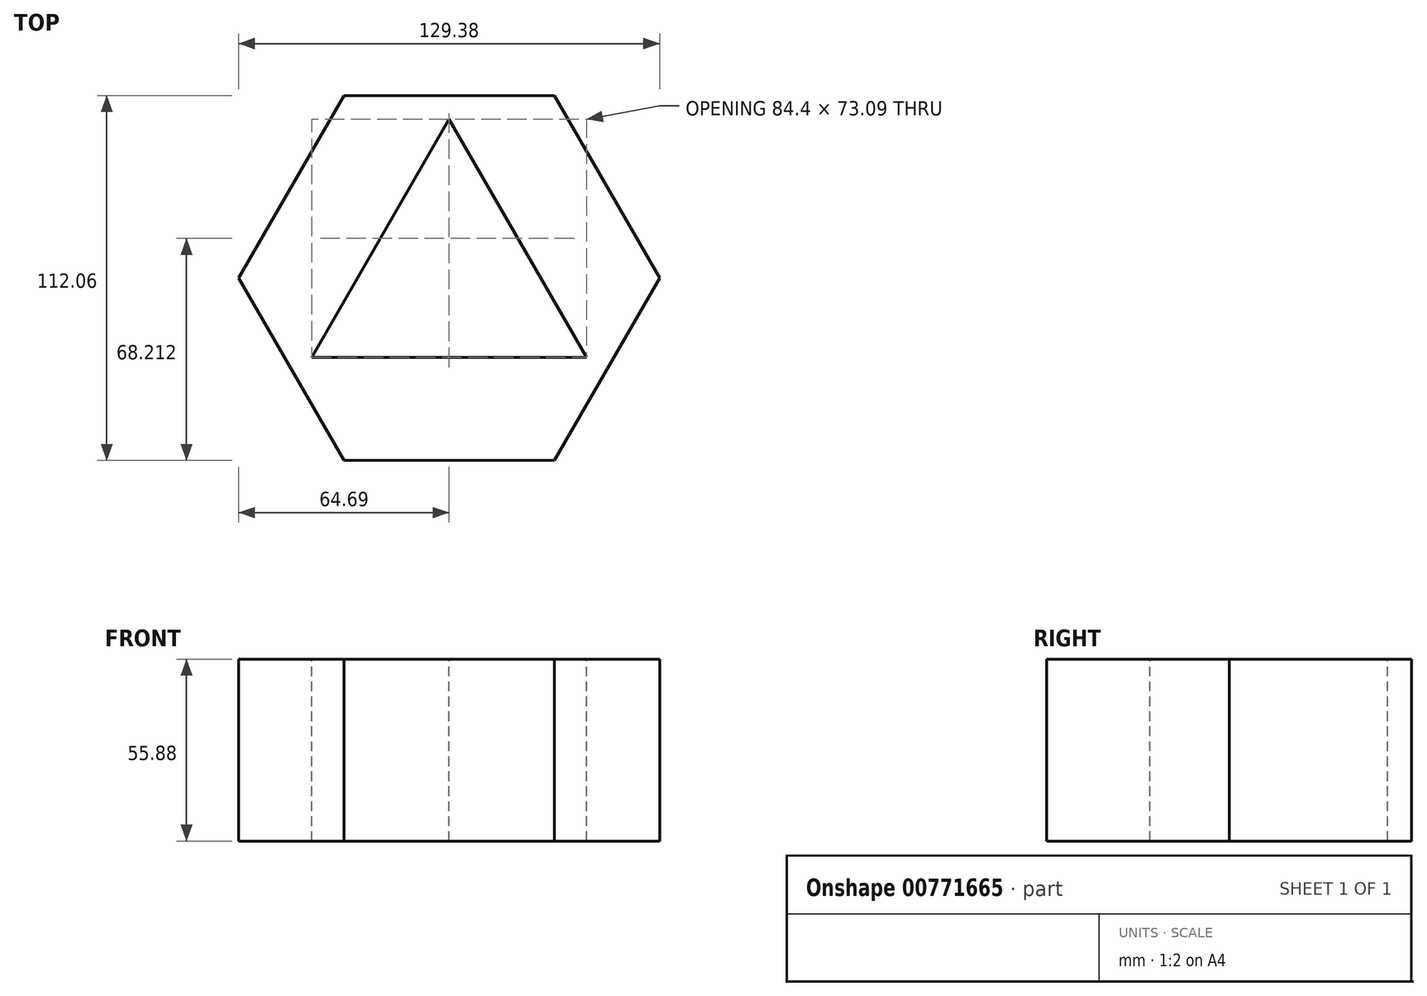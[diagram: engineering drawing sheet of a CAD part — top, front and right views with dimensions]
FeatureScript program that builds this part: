
annotation { "Feature Type Name" : "Feature", "Feature Type Description" : "" }
export const myFeature = defineFeature(function(context is Context, id is Id, definition is map)
    precondition{}
    {
        {
            var Q0;
            Q0=qCreatedBy(makeId("Top.planeOp"),FACE);
            var sketch = newSketch(context, id + "F0", { "sketchPlane" : qUnion([Q0])});
            skCircle(sketch, "E0.cCircle", {"center": v(0, 0) * mm, "radius": 56.03 * mm, "construction": true});
            skLineSegment(sketch, "E0.0", {"start": v(32.35, -56.03) * mm, "end": v(-32.35, -56.03) * mm});
            skLineSegment(sketch, "E0.1", {"start": v(-32.35, -56.03) * mm, "end": v(-64.7, 0) * mm});
            skLineSegment(sketch, "E0.2", {"start": v(-64.7, 0) * mm, "end": v(-32.35, 56.03) * mm});
            skLineSegment(sketch, "E0.3", {"start": v(-32.35, 56.03) * mm, "end": v(32.35, 56.03) * mm});
            skLineSegment(sketch, "E0.4", {"start": v(32.35, 56.03) * mm, "end": v(64.7, 0) * mm});
            skLineSegment(sketch, "E0.5", {"start": v(64.7, 0) * mm, "end": v(32.35, -56.03) * mm});
            skPoint(sketch, "E0.0.midPoint", {"position": v(0, -56.03) * mm});
            skSolve(sketch);
        }
        {
            var Q0;
            Q0 = qSketchRegion(id + "F0", true);
            extrude(context, id + "F1", {"entities" : qUnion([Q0]), "depth" : 55.88 * mm, "offsetDistance" : 25.4 * mm});
        }
        {
            var Q0;
            Q0=makeQuery(id+"F1.opExtrude","CAP_FACE",FACE,{"disambiguationData":[OSD([sQuery(id+"F0.wireOp",EDGE,"E0.0"),sQuery(id+"F0.wireOp",EDGE,"E0.1"),sQuery(id+"F0.wireOp",EDGE,"E0.2"),sQuery(id+"F0.wireOp",EDGE,"E0.3"),sQuery(id+"F0.wireOp",EDGE,"E0.4"),sQuery(id+"F0.wireOp",EDGE,"E0.5")])],"isStart":false});
            var sketch = newSketch(context, id + "F2", { "sketchPlane" : qUnion([Q0])});
            skCircle(sketch, "E1.cCircle", {"center": v(0, 0) * mm, "radius": 24.36 * mm, "construction": true});
            skLineSegment(sketch, "E1.0", {"start": v(42.2, -24.36) * mm, "end": v(-42.2, -24.36) * mm});
            skLineSegment(sketch, "E1.1", {"start": v(-42.2, -24.36) * mm, "end": v(0, 48.73) * mm});
            skLineSegment(sketch, "E1.2", {"start": v(0, 48.73) * mm, "end": v(42.2, -24.36) * mm});
            skPoint(sketch, "E1.0.midPoint", {"position": v(0, -24.36) * mm});
            skSolve(sketch);
        }
        {
            var Q0;
            Q0 = qSketchRegion(id + "F2", true);
            extrude(context, id + "F3", {"entities" : qUnion([Q0]), "operationType" : NewBodyOperationType.REMOVE, "oppositeDirection" : true, "depth" : 60.7 * mm, "offsetDistance" : 25.4 * mm});
        }
    });
